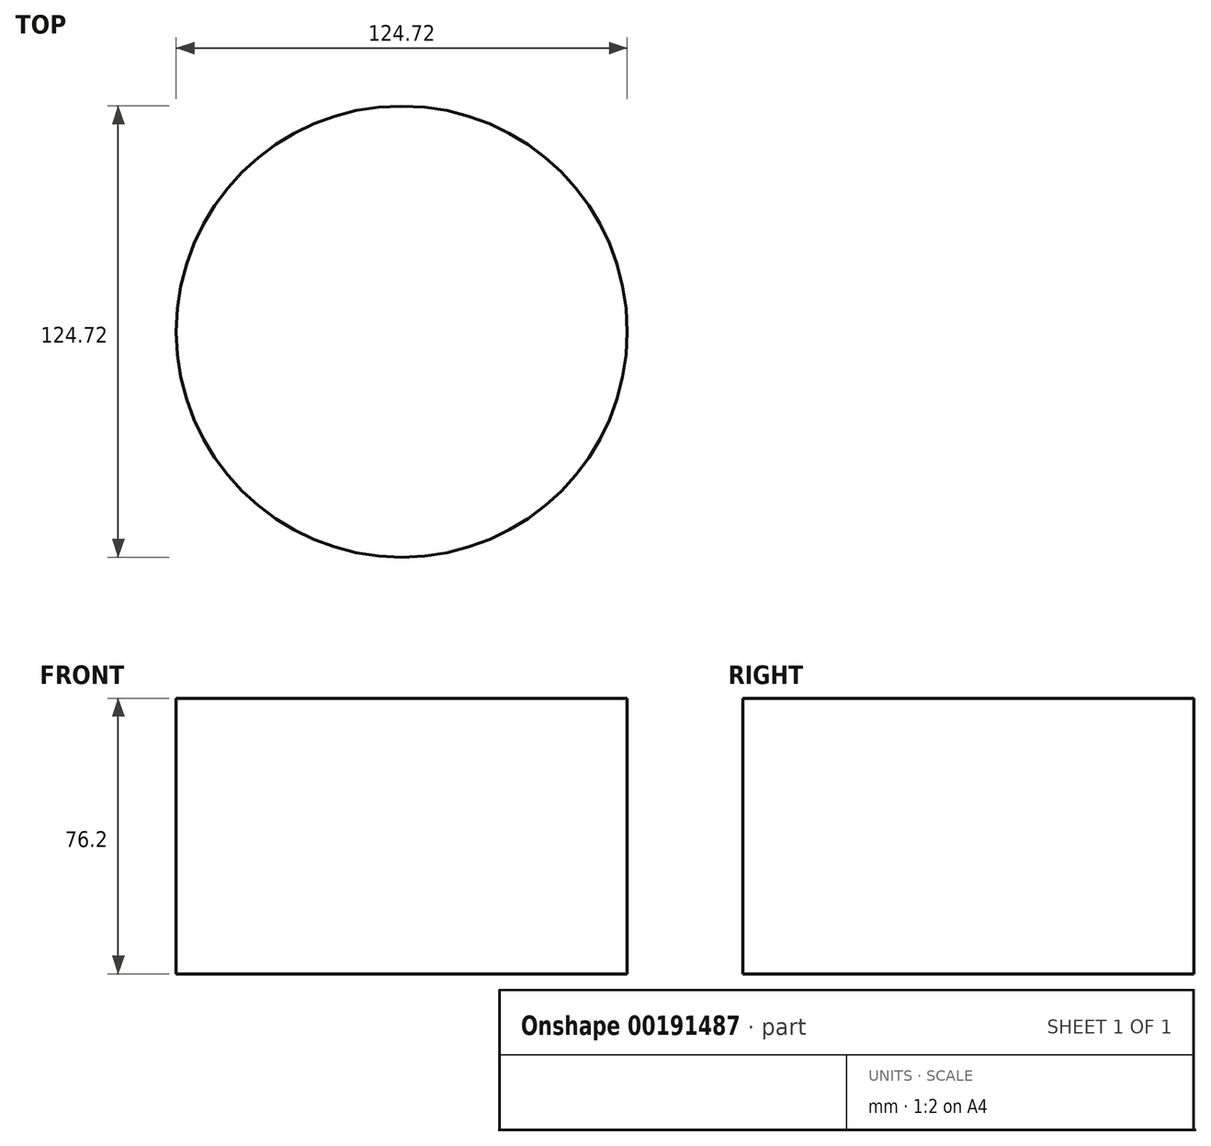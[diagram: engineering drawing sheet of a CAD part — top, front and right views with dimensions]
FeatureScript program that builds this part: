
annotation { "Feature Type Name" : "Feature", "Feature Type Description" : "" }
export const myFeature = defineFeature(function(context is Context, id is Id, definition is map)
    precondition{}
    {
        {
            var Q0;
            Q0=qCreatedBy(makeId("Top.planeOp"),FACE);
            var sketch = newSketch(context, id + "F0", { "sketchPlane" : qUnion([Q0])});
            skCircle(sketch, "E0", {"center": v(0, 0) * mm, "radius": 62.36 * mm});
            skSolve(sketch);
        }
        {
            var Q0;
            Q0=makeQuery(id+"F0.imprint","IMPRINT",FACE,{"disambiguationData":[TD([[makeQuery(id+"F0.imprint","IMPRINT",EDGE,{"derivedFrom":sQuery(id+"F0.wireOp",EDGE,"E0")}),1.0]])]});
            extrude(context, id + "F1", {"entities" : qUnion([Q0]), "depth" : 76.2 * mm});
        }
    });
